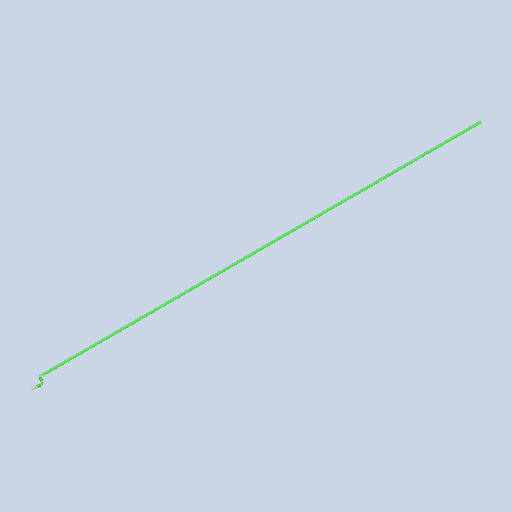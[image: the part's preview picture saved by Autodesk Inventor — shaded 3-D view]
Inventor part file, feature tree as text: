
AUTODESK INVENTOR PART (.ipt)
format: ipt  version: 2024.2 (Build 282272000, 272)  size: 83,968 bytes
history: native  units: in
note: dims shown in document units (in); Inventor stores cm internally (conversion verified against a paired STEP export)
features: sweep x1
ambient origin geometry x8: Origin, YZ Plane, XZ Plane, XY Plane, X Axis, Y Axis, Z Axis, Center Point
bodies: Solid1 (feature_tree)
feature tree (1):
  sweep  "Sweep1"
